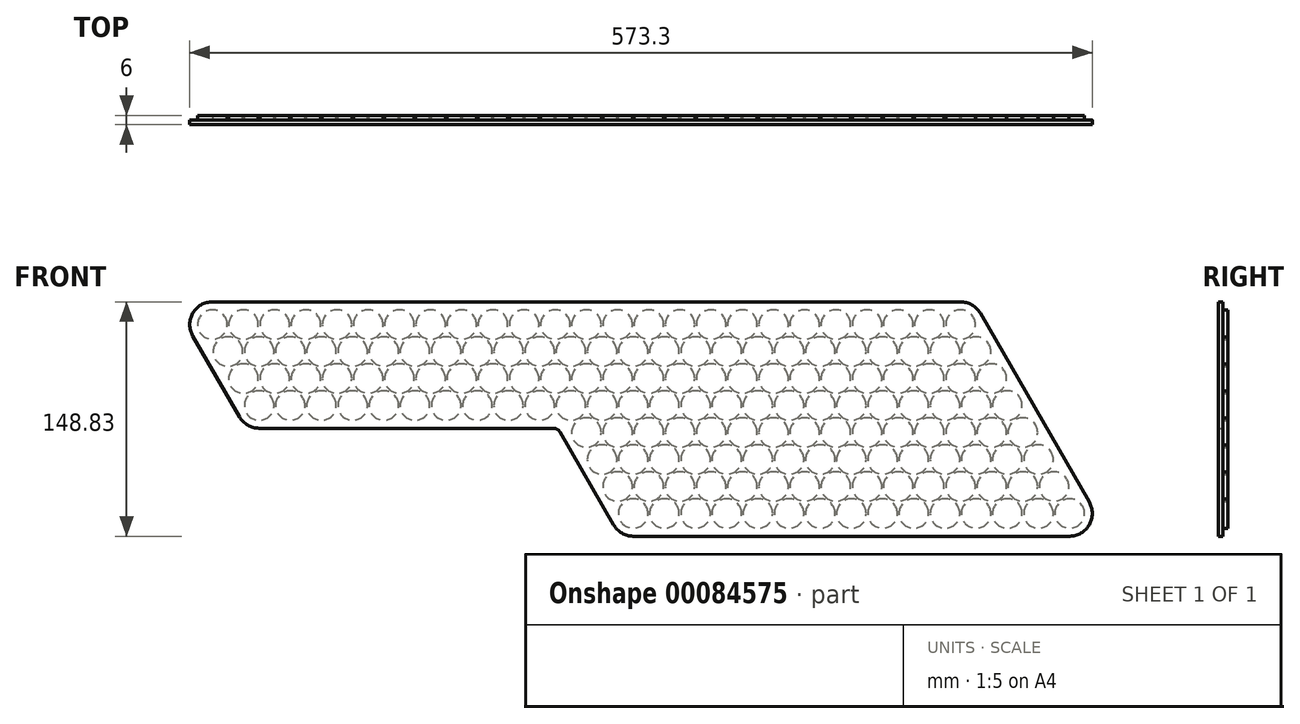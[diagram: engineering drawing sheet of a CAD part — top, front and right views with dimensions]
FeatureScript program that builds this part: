
annotation { "Feature Type Name" : "Feature", "Feature Type Description" : "" }
export const myFeature = defineFeature(function(context is Context, id is Id, definition is map)
    precondition{}
    {
        {
            var Q0;
            Q0=qCreatedBy(makeId("Front.planeOp"),FACE);
            var sketch = newSketch(context, id + "F0", { "sketchPlane" : qUnion([Q0]) });
            skCircle(sketch, "E0", {"center": v(0, 0) * mm, "radius": 9.4 * mm});
            skCircle(sketch, "E1.0.1.0", {"center": v(9.9, -17.15) * mm, "radius": 9.4 * mm});
            skCircle(sketch, "E1.0.2.0", {"center": v(19.8, -34.3) * mm, "radius": 9.4 * mm});
            skCircle(sketch, "E1.0.3.0", {"center": v(29.7, -51.44) * mm, "radius": 9.4 * mm});
            skCircle(sketch, "E1.1.0.0", {"center": v(19.8, 0) * mm, "radius": 9.4 * mm});
            skCircle(sketch, "E1.1.1.0", {"center": v(29.7, -17.15) * mm, "radius": 9.4 * mm});
            skCircle(sketch, "E1.1.2.0", {"center": v(39.6, -34.3) * mm, "radius": 9.4 * mm});
            skCircle(sketch, "E1.1.3.0", {"center": v(49.5, -51.44) * mm, "radius": 9.4 * mm});
            skCircle(sketch, "E1.2.0.0", {"center": v(39.6, 0) * mm, "radius": 9.4 * mm});
            skCircle(sketch, "E1.2.1.0", {"center": v(49.5, -17.15) * mm, "radius": 9.4 * mm});
            skCircle(sketch, "E1.2.2.0", {"center": v(59.4, -34.3) * mm, "radius": 9.4 * mm});
            skCircle(sketch, "E1.2.3.0", {"center": v(69.3, -51.44) * mm, "radius": 9.4 * mm});
            skCircle(sketch, "E1.3.0.0", {"center": v(59.4, 0) * mm, "radius": 9.4 * mm});
            skCircle(sketch, "E1.3.1.0", {"center": v(69.3, -17.15) * mm, "radius": 9.4 * mm});
            skCircle(sketch, "E1.3.2.0", {"center": v(79.2, -34.3) * mm, "radius": 9.4 * mm});
            skCircle(sketch, "E1.3.3.0", {"center": v(89.1, -51.44) * mm, "radius": 9.4 * mm});
            skCircle(sketch, "E1.4.0.0", {"center": v(79.2, 0) * mm, "radius": 9.4 * mm});
            skCircle(sketch, "E1.4.1.0", {"center": v(89.1, -17.15) * mm, "radius": 9.4 * mm});
            skCircle(sketch, "E1.4.2.0", {"center": v(99, -34.3) * mm, "radius": 9.4 * mm});
            skCircle(sketch, "E1.4.3.0", {"center": v(108.9, -51.44) * mm, "radius": 9.4 * mm});
            skCircle(sketch, "E1.5.0.0", {"center": v(99, 0) * mm, "radius": 9.4 * mm});
            skCircle(sketch, "E1.5.1.0", {"center": v(108.9, -17.15) * mm, "radius": 9.4 * mm});
            skCircle(sketch, "E1.5.2.0", {"center": v(118.8, -34.3) * mm, "radius": 9.4 * mm});
            skCircle(sketch, "E1.5.3.0", {"center": v(128.7, -51.44) * mm, "radius": 9.4 * mm});
            skCircle(sketch, "E1.6.0.0", {"center": v(118.8, 0) * mm, "radius": 9.4 * mm});
            skCircle(sketch, "E1.6.1.0", {"center": v(128.7, -17.15) * mm, "radius": 9.4 * mm});
            skCircle(sketch, "E1.6.2.0", {"center": v(138.6, -34.3) * mm, "radius": 9.4 * mm});
            skCircle(sketch, "E1.6.3.0", {"center": v(148.5, -51.44) * mm, "radius": 9.4 * mm});
            skCircle(sketch, "E1.7.0.0", {"center": v(138.6, 0) * mm, "radius": 9.4 * mm});
            skCircle(sketch, "E1.7.1.0", {"center": v(148.5, -17.15) * mm, "radius": 9.4 * mm});
            skCircle(sketch, "E1.7.2.0", {"center": v(158.4, -34.3) * mm, "radius": 9.4 * mm});
            skCircle(sketch, "E1.7.3.0", {"center": v(168.3, -51.44) * mm, "radius": 9.4 * mm});
            skCircle(sketch, "E1.8.0.0", {"center": v(158.4, 0) * mm, "radius": 9.4 * mm});
            skCircle(sketch, "E1.8.1.0", {"center": v(168.3, -17.15) * mm, "radius": 9.4 * mm});
            skCircle(sketch, "E1.8.2.0", {"center": v(178.2, -34.3) * mm, "radius": 9.4 * mm});
            skCircle(sketch, "E1.8.3.0", {"center": v(188.1, -51.44) * mm, "radius": 9.4 * mm});
            skCircle(sketch, "E1.9.0.0", {"center": v(178.2, 0) * mm, "radius": 9.4 * mm});
            skCircle(sketch, "E1.9.1.0", {"center": v(188.1, -17.15) * mm, "radius": 9.4 * mm});
            skCircle(sketch, "E1.9.2.0", {"center": v(198, -34.3) * mm, "radius": 9.4 * mm});
            skCircle(sketch, "E1.9.3.0", {"center": v(207.9, -51.44) * mm, "radius": 9.4 * mm});
            skLineSegment(sketch, "E1.direction1", {"start": v(0, 0) * mm, "end": v(19.8, 0) * mm, "construction": true});
            skLineSegment(sketch, "E1.direction2", {"start": v(0, 0) * mm, "end": v(9.9, -17.15) * mm, "construction": true});
            skCircle(sketch, "E2.0.10.0", {"center": v(198, 0) * mm, "radius": 9.4 * mm});
            skCircle(sketch, "E2.0.10.1", {"center": v(207.9, -17.15) * mm, "radius": 9.4 * mm});
            skCircle(sketch, "E2.0.10.2", {"center": v(217.8, -34.3) * mm, "radius": 9.4 * mm});
            skCircle(sketch, "E2.0.10.3", {"center": v(227.7, -51.44) * mm, "radius": 9.4 * mm});
            skCircle(sketch, "E2.0.11.0", {"center": v(217.8, 0) * mm, "radius": 9.4 * mm});
            skCircle(sketch, "E2.0.11.1", {"center": v(227.7, -17.15) * mm, "radius": 9.4 * mm});
            skCircle(sketch, "E2.0.11.2", {"center": v(237.6, -34.3) * mm, "radius": 9.4 * mm});
            skCircle(sketch, "E2.0.11.3", {"center": v(247.5, -51.44) * mm, "radius": 9.4 * mm});
            skCircle(sketch, "E2.0.12.0", {"center": v(237.6, 0) * mm, "radius": 9.4 * mm});
            skCircle(sketch, "E2.0.12.1", {"center": v(247.5, -17.15) * mm, "radius": 9.4 * mm});
            skCircle(sketch, "E2.0.12.2", {"center": v(257.4, -34.3) * mm, "radius": 9.4 * mm});
            skCircle(sketch, "E2.0.12.3", {"center": v(267.3, -51.44) * mm, "radius": 9.4 * mm});
            skCircle(sketch, "E2.0.13.0", {"center": v(257.4, 0) * mm, "radius": 9.4 * mm});
            skCircle(sketch, "E2.0.13.1", {"center": v(267.3, -17.15) * mm, "radius": 9.4 * mm});
            skCircle(sketch, "E2.0.13.2", {"center": v(277.2, -34.3) * mm, "radius": 9.4 * mm});
            skCircle(sketch, "E2.0.13.3", {"center": v(287.1, -51.44) * mm, "radius": 9.4 * mm});
            skCircle(sketch, "E2.0.14.0", {"center": v(277.2, 0) * mm, "radius": 9.4 * mm});
            skCircle(sketch, "E2.0.14.1", {"center": v(287.1, -17.15) * mm, "radius": 9.4 * mm});
            skCircle(sketch, "E2.0.14.2", {"center": v(297, -34.3) * mm, "radius": 9.4 * mm});
            skCircle(sketch, "E2.0.14.3", {"center": v(306.9, -51.44) * mm, "radius": 9.4 * mm});
            skCircle(sketch, "E2.0.15.0", {"center": v(297, 0) * mm, "radius": 9.4 * mm});
            skCircle(sketch, "E2.0.15.1", {"center": v(306.9, -17.15) * mm, "radius": 9.4 * mm});
            skCircle(sketch, "E2.0.15.2", {"center": v(316.8, -34.3) * mm, "radius": 9.4 * mm});
            skCircle(sketch, "E2.0.15.3", {"center": v(326.7, -51.44) * mm, "radius": 9.4 * mm});
            skCircle(sketch, "E2.0.16.0", {"center": v(316.8, 0) * mm, "radius": 9.4 * mm});
            skCircle(sketch, "E2.0.16.1", {"center": v(326.7, -17.15) * mm, "radius": 9.4 * mm});
            skCircle(sketch, "E2.0.16.2", {"center": v(336.6, -34.3) * mm, "radius": 9.4 * mm});
            skCircle(sketch, "E2.0.16.3", {"center": v(346.5, -51.44) * mm, "radius": 9.4 * mm});
            skCircle(sketch, "E2.0.17.0", {"center": v(336.6, 0) * mm, "radius": 9.4 * mm});
            skCircle(sketch, "E2.0.17.1", {"center": v(346.5, -17.15) * mm, "radius": 9.4 * mm});
            skCircle(sketch, "E2.0.17.2", {"center": v(356.4, -34.3) * mm, "radius": 9.4 * mm});
            skCircle(sketch, "E2.0.17.3", {"center": v(366.3, -51.44) * mm, "radius": 9.4 * mm});
            skCircle(sketch, "E2.0.18.0", {"center": v(356.4, 0) * mm, "radius": 9.4 * mm});
            skCircle(sketch, "E2.0.18.1", {"center": v(366.3, -17.15) * mm, "radius": 9.4 * mm});
            skCircle(sketch, "E2.0.18.2", {"center": v(376.2, -34.3) * mm, "radius": 9.4 * mm});
            skCircle(sketch, "E2.0.18.3", {"center": v(386.1, -51.44) * mm, "radius": 9.4 * mm});
            skCircle(sketch, "E2.0.19.0", {"center": v(376.2, 0) * mm, "radius": 9.4 * mm});
            skCircle(sketch, "E2.0.19.1", {"center": v(386.1, -17.15) * mm, "radius": 9.4 * mm});
            skCircle(sketch, "E2.0.19.2", {"center": v(396, -34.3) * mm, "radius": 9.4 * mm});
            skCircle(sketch, "E2.0.19.3", {"center": v(405.9, -51.44) * mm, "radius": 9.4 * mm});
            skCircle(sketch, "E3.0.20.0", {"center": v(396, 0) * mm, "radius": 9.4 * mm});
            skCircle(sketch, "E3.0.20.1", {"center": v(405.9, -17.15) * mm, "radius": 9.4 * mm});
            skCircle(sketch, "E3.0.20.2", {"center": v(415.8, -34.3) * mm, "radius": 9.4 * mm});
            skCircle(sketch, "E3.0.20.3", {"center": v(425.7, -51.44) * mm, "radius": 9.4 * mm});
            skCircle(sketch, "E3.0.21.0", {"center": v(415.8, 0) * mm, "radius": 9.4 * mm});
            skCircle(sketch, "E3.0.21.1", {"center": v(425.7, -17.15) * mm, "radius": 9.4 * mm});
            skCircle(sketch, "E3.0.21.2", {"center": v(435.6, -34.3) * mm, "radius": 9.4 * mm});
            skCircle(sketch, "E3.0.21.3", {"center": v(445.5, -51.44) * mm, "radius": 9.4 * mm});
            skCircle(sketch, "E3.0.22.0", {"center": v(435.6, 0) * mm, "radius": 9.4 * mm});
            skCircle(sketch, "E3.0.22.1", {"center": v(445.5, -17.15) * mm, "radius": 9.4 * mm});
            skCircle(sketch, "E3.0.22.2", {"center": v(455.4, -34.3) * mm, "radius": 9.4 * mm});
            skCircle(sketch, "E3.0.22.3", {"center": v(465.3, -51.44) * mm, "radius": 9.4 * mm});
            skCircle(sketch, "E3.0.23.0", {"center": v(455.4, 0) * mm, "radius": 9.4 * mm});
            skCircle(sketch, "E3.0.23.1", {"center": v(465.3, -17.15) * mm, "radius": 9.4 * mm});
            skCircle(sketch, "E3.0.23.2", {"center": v(475.2, -34.3) * mm, "radius": 9.4 * mm});
            skCircle(sketch, "E3.0.23.3", {"center": v(485.1, -51.44) * mm, "radius": 9.4 * mm});
            skCircle(sketch, "E3.0.24.0", {"center": v(475.2, 0) * mm, "radius": 9.4 * mm});
            skCircle(sketch, "E3.0.24.1", {"center": v(485.1, -17.15) * mm, "radius": 9.4 * mm});
            skCircle(sketch, "E3.0.24.2", {"center": v(495, -34.3) * mm, "radius": 9.4 * mm});
            skCircle(sketch, "E3.0.24.3", {"center": v(504.9, -51.44) * mm, "radius": 9.4 * mm});
            skLineSegment(sketch, "E4", {"start": v(227.7, -51.44) * mm, "end": v(198, 0) * mm, "construction": true});
            skLineSegment(sketch, "E5", {"start": v(277.2, 0) * mm, "end": v(247.5, -51.44) * mm, "construction": true});
            skLineSegment(sketch, "E6", {"start": v(227.7, -51.44) * mm, "end": v(247.5, -85.74) * mm, "construction": true});
            skLineSegment(sketch, "E7", {"start": v(247.5, -51.44) * mm, "end": v(227.7, -85.74) * mm, "construction": true});
            skCircle(sketch, "E8", {"center": v(237.6, -68.59) * mm, "radius": 9.4 * mm});
            skCircle(sketch, "E9.0.1.0", {"center": v(247.5, -85.74) * mm, "radius": 9.4 * mm});
            skCircle(sketch, "E9.0.2.0", {"center": v(257.4, -102.88) * mm, "radius": 9.4 * mm});
            skCircle(sketch, "E9.0.3.0", {"center": v(267.3, -120.03) * mm, "radius": 9.4 * mm});
            skCircle(sketch, "E9.1.0.0", {"center": v(257.4, -68.59) * mm, "radius": 9.4 * mm});
            skCircle(sketch, "E9.1.1.0", {"center": v(267.3, -85.74) * mm, "radius": 9.4 * mm});
            skCircle(sketch, "E9.1.2.0", {"center": v(277.2, -102.88) * mm, "radius": 9.4 * mm});
            skCircle(sketch, "E9.1.3.0", {"center": v(287.1, -120.03) * mm, "radius": 9.4 * mm});
            skCircle(sketch, "E9.2.0.0", {"center": v(277.2, -68.59) * mm, "radius": 9.4 * mm});
            skCircle(sketch, "E9.2.1.0", {"center": v(287.1, -85.74) * mm, "radius": 9.4 * mm});
            skCircle(sketch, "E9.2.2.0", {"center": v(297, -102.88) * mm, "radius": 9.4 * mm});
            skCircle(sketch, "E9.2.3.0", {"center": v(306.9, -120.03) * mm, "radius": 9.4 * mm});
            skCircle(sketch, "E9.3.0.0", {"center": v(297, -68.59) * mm, "radius": 9.4 * mm});
            skCircle(sketch, "E9.3.1.0", {"center": v(306.9, -85.74) * mm, "radius": 9.4 * mm});
            skCircle(sketch, "E9.3.2.0", {"center": v(316.8, -102.88) * mm, "radius": 9.4 * mm});
            skCircle(sketch, "E9.3.3.0", {"center": v(326.7, -120.03) * mm, "radius": 9.4 * mm});
            skCircle(sketch, "E9.4.0.0", {"center": v(316.8, -68.59) * mm, "radius": 9.4 * mm});
            skCircle(sketch, "E9.4.1.0", {"center": v(326.7, -85.74) * mm, "radius": 9.4 * mm});
            skCircle(sketch, "E9.4.2.0", {"center": v(336.6, -102.88) * mm, "radius": 9.4 * mm});
            skCircle(sketch, "E9.4.3.0", {"center": v(346.5, -120.03) * mm, "radius": 9.4 * mm});
            skCircle(sketch, "E9.5.0.0", {"center": v(336.6, -68.59) * mm, "radius": 9.4 * mm});
            skCircle(sketch, "E9.5.1.0", {"center": v(346.5, -85.74) * mm, "radius": 9.4 * mm});
            skCircle(sketch, "E9.5.2.0", {"center": v(356.4, -102.88) * mm, "radius": 9.4 * mm});
            skCircle(sketch, "E9.5.3.0", {"center": v(366.3, -120.03) * mm, "radius": 9.4 * mm});
            skCircle(sketch, "E9.6.0.0", {"center": v(356.4, -68.59) * mm, "radius": 9.4 * mm});
            skCircle(sketch, "E9.6.1.0", {"center": v(366.3, -85.74) * mm, "radius": 9.4 * mm});
            skCircle(sketch, "E9.6.2.0", {"center": v(376.2, -102.88) * mm, "radius": 9.4 * mm});
            skCircle(sketch, "E9.6.3.0", {"center": v(386.1, -120.03) * mm, "radius": 9.4 * mm});
            skCircle(sketch, "E9.7.0.0", {"center": v(376.2, -68.59) * mm, "radius": 9.4 * mm});
            skCircle(sketch, "E9.7.1.0", {"center": v(386.1, -85.74) * mm, "radius": 9.4 * mm});
            skCircle(sketch, "E9.7.2.0", {"center": v(396, -102.88) * mm, "radius": 9.4 * mm});
            skCircle(sketch, "E9.7.3.0", {"center": v(405.9, -120.03) * mm, "radius": 9.4 * mm});
            skCircle(sketch, "E9.8.0.0", {"center": v(396, -68.59) * mm, "radius": 9.4 * mm});
            skCircle(sketch, "E9.8.1.0", {"center": v(405.9, -85.74) * mm, "radius": 9.4 * mm});
            skCircle(sketch, "E9.8.2.0", {"center": v(415.8, -102.88) * mm, "radius": 9.4 * mm});
            skCircle(sketch, "E9.8.3.0", {"center": v(425.7, -120.03) * mm, "radius": 9.4 * mm});
            skCircle(sketch, "E9.9.0.0", {"center": v(415.8, -68.59) * mm, "radius": 9.4 * mm});
            skCircle(sketch, "E9.9.1.0", {"center": v(425.7, -85.74) * mm, "radius": 9.4 * mm});
            skCircle(sketch, "E9.9.2.0", {"center": v(435.6, -102.88) * mm, "radius": 9.4 * mm});
            skCircle(sketch, "E9.9.3.0", {"center": v(445.5, -120.03) * mm, "radius": 9.4 * mm});
            skCircle(sketch, "E9.10.0.0", {"center": v(435.6, -68.59) * mm, "radius": 9.4 * mm});
            skCircle(sketch, "E9.10.1.0", {"center": v(445.5, -85.74) * mm, "radius": 9.4 * mm});
            skCircle(sketch, "E9.10.2.0", {"center": v(455.4, -102.88) * mm, "radius": 9.4 * mm});
            skCircle(sketch, "E9.10.3.0", {"center": v(465.3, -120.03) * mm, "radius": 9.4 * mm});
            skCircle(sketch, "E9.11.0.0", {"center": v(455.4, -68.59) * mm, "radius": 9.4 * mm});
            skCircle(sketch, "E9.11.1.0", {"center": v(465.3, -85.74) * mm, "radius": 9.4 * mm});
            skCircle(sketch, "E9.11.2.0", {"center": v(475.2, -102.88) * mm, "radius": 9.4 * mm});
            skCircle(sketch, "E9.11.3.0", {"center": v(485.1, -120.03) * mm, "radius": 9.4 * mm});
            skCircle(sketch, "E9.12.0.0", {"center": v(475.2, -68.59) * mm, "radius": 9.4 * mm});
            skCircle(sketch, "E9.12.1.0", {"center": v(485.1, -85.74) * mm, "radius": 9.4 * mm});
            skCircle(sketch, "E9.12.2.0", {"center": v(495, -102.88) * mm, "radius": 9.4 * mm});
            skCircle(sketch, "E9.12.3.0", {"center": v(504.9, -120.03) * mm, "radius": 9.4 * mm});
            skCircle(sketch, "E9.13.0.0", {"center": v(495, -68.59) * mm, "radius": 9.4 * mm});
            skCircle(sketch, "E9.13.1.0", {"center": v(504.9, -85.74) * mm, "radius": 9.4 * mm});
            skCircle(sketch, "E9.13.2.0", {"center": v(514.8, -102.88) * mm, "radius": 9.4 * mm});
            skCircle(sketch, "E9.13.3.0", {"center": v(524.7, -120.03) * mm, "radius": 9.4 * mm});
            skLineSegment(sketch, "E9.direction1", {"start": v(237.6, -68.59) * mm, "end": v(257.4, -68.59) * mm, "construction": true});
            skLineSegment(sketch, "E9.direction2", {"start": v(237.6, -68.59) * mm, "end": v(247.5, -85.74) * mm, "construction": true});
            skCircle(sketch, "E10.0.14.0", {"center": v(514.8, -68.59) * mm, "radius": 9.4 * mm});
            skCircle(sketch, "E10.0.14.1", {"center": v(524.7, -85.74) * mm, "radius": 9.4 * mm});
            skCircle(sketch, "E10.0.14.2", {"center": v(534.6, -102.88) * mm, "radius": 9.4 * mm});
            skCircle(sketch, "E10.0.14.3", {"center": v(544.5, -120.03) * mm, "radius": 9.4 * mm});
            skSolve(sketch);
        }
        {
            var Q0;
            Q0 = qSketchRegion(id + "F0", true);
            extrude(context, id + "F1", {"entities" : qUnion([Q0]), "depth" : 3 * mm});
        }
        {
            var Q0;
            Q0=makeQuery(id+"F1.opExtrude","CAP_FACE",FACE,{"disambiguationData":[OSD([sQuery(id+"F0.wireOp",EDGE,"E0")])],"isStart":false});
            var sketch = newSketch(context, id + "F2", { "sketchPlane" : qUnion([Q0]) });
            skCircle(sketch, "E11.0", {"center": v(0, 0) * mm, "radius": 9.4 * mm});
            skCircle(sketch, "E11.1", {"center": v(29.7, -51.44) * mm, "radius": 9.4 * mm});
            skCircle(sketch, "E11.2", {"center": v(475.2, 0) * mm, "radius": 9.4 * mm});
            skCircle(sketch, "E11.3", {"center": v(544.5, -120.03) * mm, "radius": 9.4 * mm});
            skCircle(sketch, "E11.4", {"center": v(267.3, -120.03) * mm, "radius": 9.4 * mm});
            skCircle(sketch, "E11.5", {"center": v(237.6, -68.59) * mm, "radius": 9.4 * mm});
            skCircle(sketch, "E11.6", {"center": v(227.7, -51.44) * mm, "radius": 9.4 * mm});
            skCircle(sketch, "E12.0", {"center": v(0, 0) * mm, "radius": 14.4 * mm});
            skCircle(sketch, "E13.0", {"center": v(475.2, 0) * mm, "radius": 14.4 * mm});
            skCircle(sketch, "E14.0", {"center": v(544.5, -120.03) * mm, "radius": 14.4 * mm});
            skCircle(sketch, "E15.0", {"center": v(267.3, -120.03) * mm, "radius": 14.4 * mm});
            skCircle(sketch, "E16.0", {"center": v(29.7, -51.44) * mm, "radius": 14.4 * mm});
            skLineSegment(sketch, "E17", {"start": v(0, 14.4) * mm, "end": v(475.2, 14.4) * mm});
            skLineSegment(sketch, "E18", {"start": v(487.67, 7.2) * mm, "end": v(556.97, -112.83) * mm});
            skLineSegment(sketch, "E19", {"start": v(544.5, -134.43) * mm, "end": v(267.3, -134.43) * mm});
            skLineSegment(sketch, "E20", {"start": v(-12.47, -7.2) * mm, "end": v(17.23, -58.64) * mm});
            skLineSegment(sketch, "E21", {"start": v(29.7, -65.84) * mm, "end": v(219.39, -65.84) * mm});
            skLineSegment(sketch, "E22", {"start": v(219.39, -65.84) * mm, "end": v(254.83, -127.23) * mm});
            skSolve(sketch);
        }
        {
            var Q0;
            Q0 = qSketchRegion(id + "F2", true);
            var Q1;
            Q1=makeQuery(id+"F2.imprint","IMPRINT",FACE,{"disambiguationData":[TD([[makeQuery(id+"F2.imprint","IMPRINT",EDGE,{"derivedFrom":sQuery(id+"F2.wireOp",EDGE,"E11.2")}),1.0]])]});
            var Q2;
            Q2=makeQuery(id+"F2.imprint","IMPRINT",FACE,{"disambiguationData":[TD([[makeQuery(id+"F2.imprint","IMPRINT",EDGE,{"derivedFrom":sQuery(id+"F2.wireOp",EDGE,"E11.0")}),1.0]])]});
            var Q3;
            Q3=makeQuery(id+"F2.imprint","IMPRINT",FACE,{"disambiguationData":[TD([[makeQuery(id+"F2.imprint","IMPRINT",EDGE,{"derivedFrom":sQuery(id+"F2.wireOp",EDGE,"E11.1")}),1.0]])]});
            var Q4;
            Q4=makeQuery(id+"F2.imprint","IMPRINT",FACE,{"disambiguationData":[TD([[makeQuery(id+"F2.imprint","IMPRINT",EDGE,{"derivedFrom":sQuery(id+"F2.wireOp",EDGE,"E11.6")}),1.0]])]});
            var Q5;
            Q5=makeQuery(id+"F2.imprint","IMPRINT",FACE,{"disambiguationData":[TD([[makeQuery(id+"F2.imprint","IMPRINT",EDGE,{"derivedFrom":sQuery(id+"F2.wireOp",EDGE,"E11.5")}),1.0]])]});
            var Q6;
            Q6=makeQuery(id+"F2.imprint","IMPRINT",FACE,{"disambiguationData":[TD([[makeQuery(id+"F2.imprint","IMPRINT",EDGE,{"derivedFrom":sQuery(id+"F2.wireOp",EDGE,"E11.4")}),1.0]])]});
            var Q7;
            Q7=makeQuery(id+"F2.imprint","IMPRINT",FACE,{"disambiguationData":[TD([[makeQuery(id+"F2.imprint","IMPRINT",EDGE,{"derivedFrom":sQuery(id+"F2.wireOp",EDGE,"E11.3")}),1.0]])]});
            extrude(context, id + "F3", {"entities" : qUnion([Q0, Q1, Q2, Q3, Q4, Q5, Q6, Q7]), "depth" : 3 * mm});
        }
        {
            var Q0;
            Q0=makeQuery(id+"F3.opExtrude","SWEPT_EDGE",EDGE,{"disambiguationData":[OSD([sQuery(id+"F2.wireOp",EDGE,"E21"),sQuery(id+"F2.wireOp",EDGE,"E22")])]});
            fillet(context, id + "F4", {"entities" : qUnion([Q0]), "radius" : 5 * mm, "tangentPropagation" : true, "conicFillet" : false});
        }
    });
